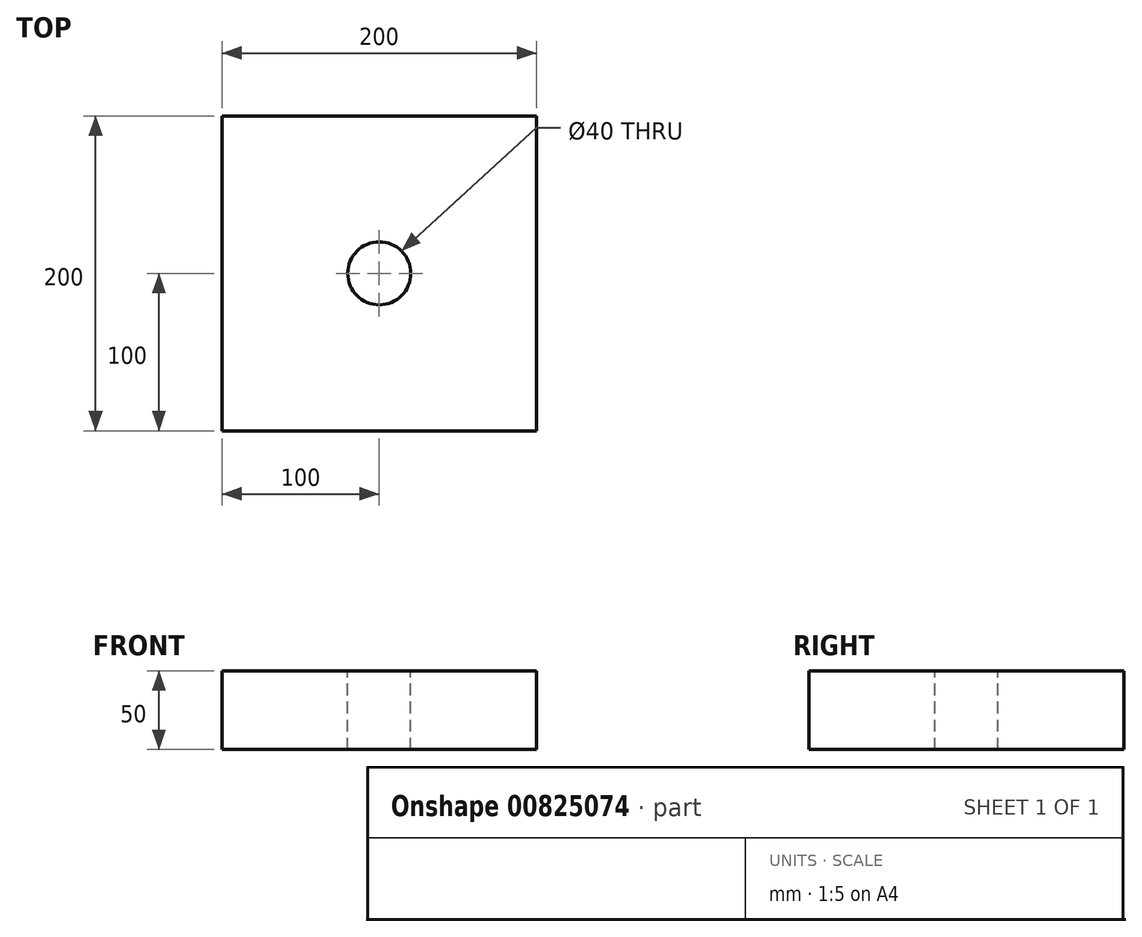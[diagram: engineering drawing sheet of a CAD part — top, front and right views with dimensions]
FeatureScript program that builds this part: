
annotation { "Feature Type Name" : "Feature", "Feature Type Description" : "" }
export const myFeature = defineFeature(function(context is Context, id is Id, definition is map)
    precondition{}
    {
        {
            var Q0;
            Q0=qCreatedBy(makeId("Top.planeOp"),FACE);
            var sketch = newSketch(context, id + "F0", { "sketchPlane" : qUnion([Q0])});
            skCircle(sketch, "E0", {"center": v(0, 0) * mm, "radius": 20 * mm});
            skLineSegment(sketch, "E1.bottom", {"start": v(-100, 100) * mm, "end": v(100, 100) * mm});
            skLineSegment(sketch, "E1.top", {"start": v(-100, -100) * mm, "end": v(100, -100) * mm});
            skLineSegment(sketch, "E1.left", {"start": v(-100, 100) * mm, "end": v(-100, -100) * mm});
            skLineSegment(sketch, "E1.right", {"start": v(100, 100) * mm, "end": v(100, -100) * mm});
            skSolve(sketch);
        }
        {
            var Q0;
            Q0=makeQuery(id+"F0.imprint","IMPRINT",FACE,{"disambiguationData":[TD([[makeQuery(id+"F0.imprint","IMPRINT",EDGE,{"derivedFrom":sQuery(id+"F0.wireOp",EDGE,"E0")}),-1.0]])]});
            extrude(context, id + "F1", {"entities" : qUnion([Q0]), "oppositeDirection" : true, "depth" : 50 * mm, "offsetDistance" : 25 * mm});
        }
    });
